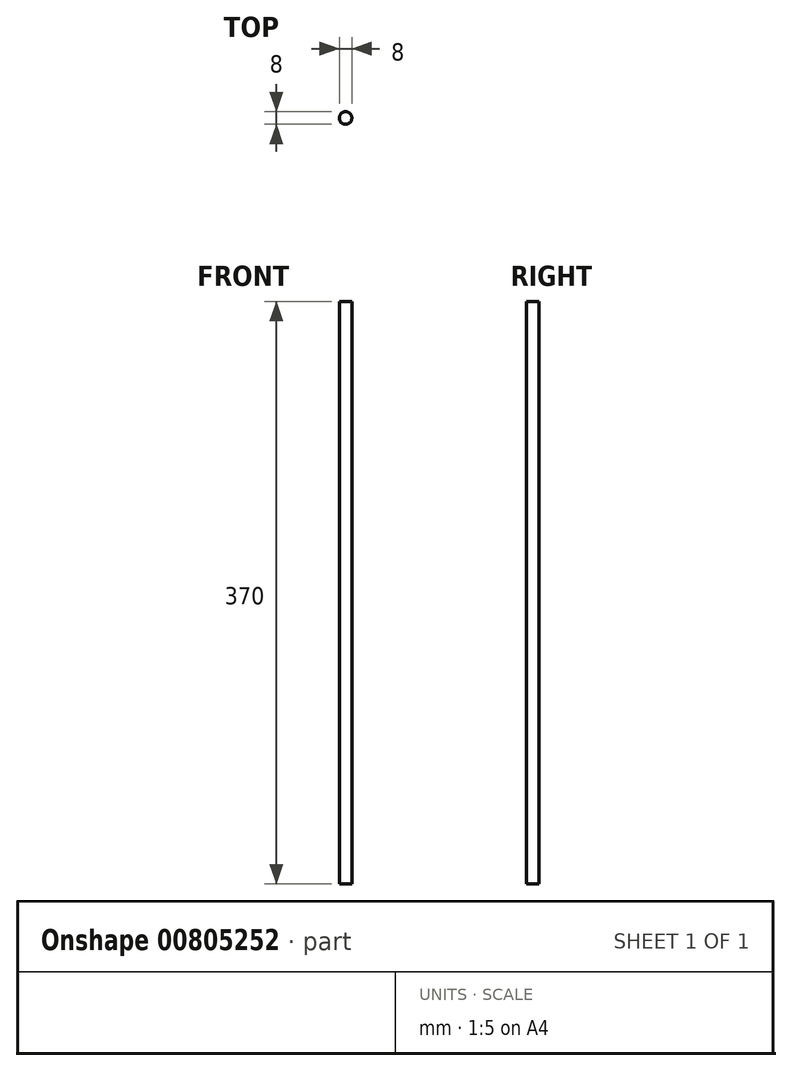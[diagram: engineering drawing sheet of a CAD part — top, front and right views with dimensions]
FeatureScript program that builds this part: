
annotation { "Feature Type Name" : "Feature", "Feature Type Description" : "" }
export const myFeature = defineFeature(function(context is Context, id is Id, definition is map)
    precondition{}
    {
        {
            var Q0;
            Q0=qCreatedBy(makeId("Front.planeOp"),FACE);
            var sketch = newSketch(context, id + "F0", { "sketchPlane" : qUnion([Q0])});
            skLineSegment(sketch, "E0.bottom", {"start": v(0, 185) * mm, "end": v(-4, 185) * mm});
            skLineSegment(sketch, "E0.top", {"start": v(0, -185) * mm, "end": v(-4, -185) * mm});
            skLineSegment(sketch, "E0.left", {"start": v(0, 185) * mm, "end": v(0, -185) * mm});
            skLineSegment(sketch, "E0.right", {"start": v(-4, 185) * mm, "end": v(-4, -185) * mm});
            skSolve(sketch);
        }
        {
            var Q0;
            Q0=makeQuery(id+"F0.imprint","IMPRINT",FACE,{"disambiguationData":[TD([[makeQuery(id+"F0.imprint","IMPRINT",EDGE,{"derivedFrom":sQuery(id+"F0.wireOp",EDGE,"E0.bottom")}),1.0]])]});
            var Q1;
            Q1=sQuery(id+"F0.wireOp",EDGE,"E0.left");
            revolve(context, id + "F1", {"surfaceOperationType" : NewSurfaceOperationType.NEW, "entities" : qUnion([Q0]), "axis" : qUnion([Q1]), "revolveType" : RevolveType.FULL});
        }
    });
